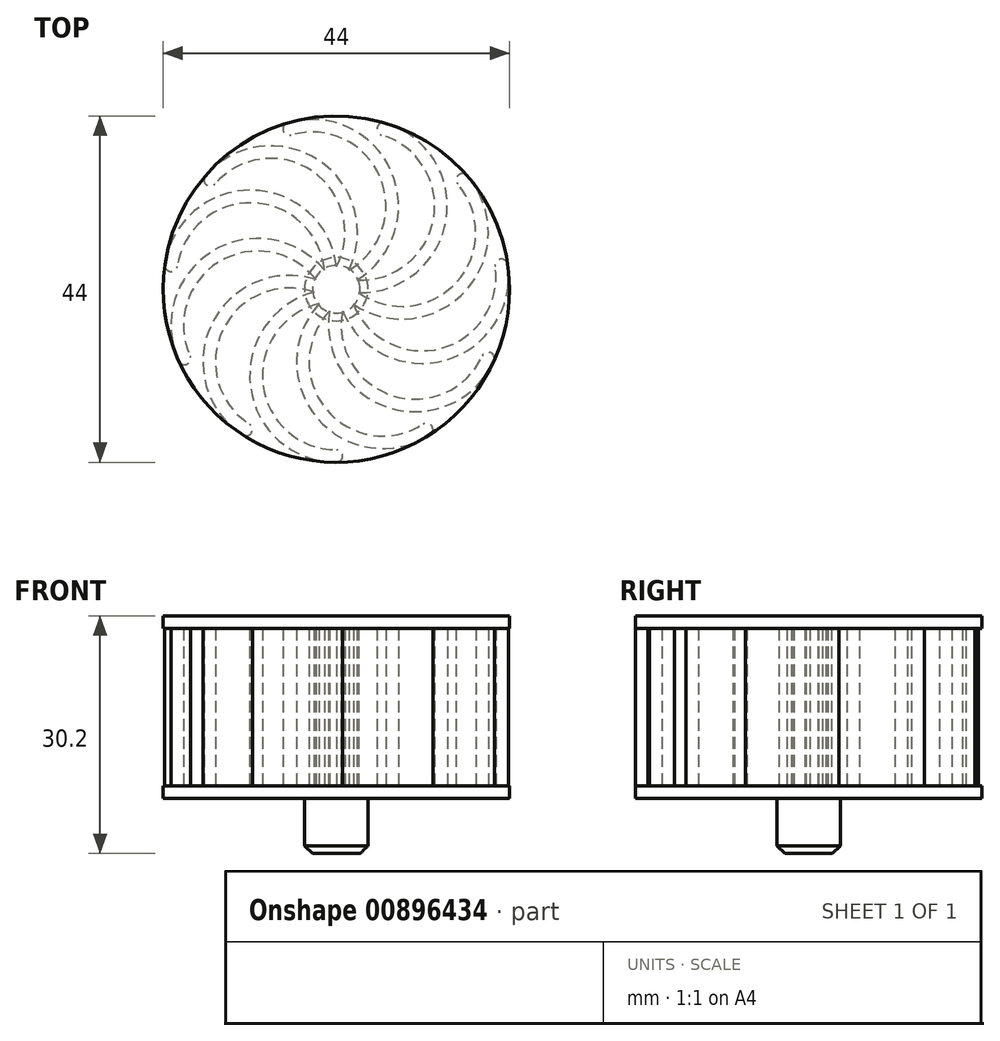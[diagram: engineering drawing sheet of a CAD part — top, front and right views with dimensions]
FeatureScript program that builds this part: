
annotation { "Feature Type Name" : "Feature", "Feature Type Description" : "" }
export const myFeature = defineFeature(function(context is Context, id is Id, definition is map)
    precondition{}
    {
        {
            assignVariable(context, id + "F0", {"name" : "mountingHeight", "anyValue" : 7 * mm});
        }
        {
            assignVariable(context, id + "F1", {"name" : "height", "anyValue" : 20 * mm});
        }
        {
            assignVariable(context, id + "F2", {"name" : "wall", "anyValue" : 1.6 * mm});
        }
        {
            assignVariable(context, id + "F3", {"name" : "blades", "anyValue" : 11});
        }
        {
            var Q0;
            Q0=qCreatedBy(makeId("Top.planeOp"),FACE);
            var sketch = newSketch(context, id + "F4", { "sketchPlane" : qUnion([Q0])});
            skCircle(sketch, "E0", {"center": v(0, 0) * mm, "radius": 22 * mm});
            skCircle(sketch, "E1", {"center": v(0, 0) * mm, "radius": 4.03 * mm});
            skSolve(sketch);
        }
        {
            var Q0;
            Q0=makeQuery(id+"F4.imprint","IMPRINT",FACE,{"disambiguationData":[TD([[makeQuery(id+"F4.imprint","IMPRINT",EDGE,{"derivedFrom":sQuery(id+"F4.wireOp",EDGE,"E0")}),1.0]])]});
            var Q1;
            Q1=makeQuery(id+"F4.imprint","IMPRINT",FACE,{"disambiguationData":[TD([[makeQuery(id+"F4.imprint","IMPRINT",EDGE,{"derivedFrom":sQuery(id+"F4.wireOp",EDGE,"E1")}),1.0]])]});
            extrude(context, id + "F5", {"entities" : qUnion([Q0, Q1]), "depth" : getVariable(context, 'wall'), "offsetDistance" : 25 * mm});
        }
        {
            var Q0;
            Q0=makeQuery(id+"F4.imprint","IMPRINT",FACE,{"disambiguationData":[TD([[makeQuery(id+"F4.imprint","IMPRINT",EDGE,{"derivedFrom":sQuery(id+"F4.wireOp",EDGE,"E1")}),1.0]])]});
            extrude(context, id + "F6", {"entities" : qUnion([Q0]), "operationType" : NewBodyOperationType.ADD, "oppositeDirection" : true, "depth" : getVariable(context, 'mountingHeight'), "offsetDistance" : 25 * mm});
        }
        {
            var Q0;
            Q0=makeQuery(id+"F5.opExtrude","CAP_FACE",FACE,{"disambiguationData":[OSD([sQuery(id+"F4.wireOp",EDGE,"E0")])],"isStart":false});
            var sketch = newSketch(context, id + "F7", { "sketchPlane" : qUnion([Q0])});
            skArc(sketch, "E2", {"start": v(0, 0) * mm, "mid": v(-11, -11) * mm, "end": v(0, -22) * mm});
            skArc(sketch, "E3.0", {"start": v(0, -1.6) * mm, "mid": v(-9.4, -11) * mm, "end": v(0, -20.4) * mm});
            skArc(sketch, "E4", {"start": v(0, 0) * mm, "mid": v(0.8, -0.8) * mm, "end": v(0, -1.6) * mm});
            skArc(sketch, "E5", {"start": v(0, -20.4) * mm, "mid": v(0.8, -21.2) * mm, "end": v(0, -22) * mm});
            skSolve(sketch);
        }
        {
            var Q0;
            Q0=makeQuery(id+"F6.opExtrude","CAP_EDGE",EDGE,{"disambiguationData":[OSD([sQuery(id+"F4.wireOp",EDGE,"E1")])],"isStart":false});
            chamfer(context, id + "F8", {"entities" : qUnion([Q0]), "width" : 1 * mm, "tangentPropagation" : true});
        }
        {
            var Q0;
            {var subQ4=sQuery(id+"F7.wireOp",EDGE,"E2");Q0=makeQuery(id+"F7.imprint","IMPRINT",FACE,{"disambiguationData":[TD([[makeQuery(id+"F7.imprint","IMPRINT",EDGE,{"derivedFrom":subQ4}),1.0]])]});}
            extrude(context, id + "F9", {"entities" : qUnion([Q0]), "depth" : getVariable(context, 'height'), "offsetDistance" : 25 * mm});
        }
        {
            var Q0;
            Q0=makeQuery(id+"F9.opExtrude","SWEPT_BODY",BODY,{"disambiguationData":[OSD([sQuery(id+"F4.wireOp",EDGE,"E0"),sQuery(id+"F7.wireOp",EDGE,"E2"),sQuery(id+"F7.wireOp",EDGE,"d03e0ac7-ecf9-454f-a7f5-ac63b770d9b9.0"),sQuery(id+"F7.wireOp",EDGE,"87743ef1-c0a4-470f-af4a-e0fff581d53f"),sQuery(id+"F7.wireOp",EDGE,"098a4024-eb5d-4de3-bc97-1e13fd1b39a1")])]});
            var Q1;
            Q1=makeQuery(id+"F6.opExtrude","SWEPT_FACE",FACE,{"disambiguationData":[OSD([sQuery(id+"F4.wireOp",EDGE,"E1")])]});
            circularPattern(context, id + "F10", {"operationType" : NewBodyOperationType.ADD, "entities" : qUnion([Q0]), "axis" : qUnion([Q1]), "angle" : 360 * degree, "instanceCount" : getVariable(context, 'blades'), "equalSpace" : true});
        }
        {
            var Q0;
            Q0=makeQuery(id+"F4.imprint","IMPRINT",FACE,{"disambiguationData":[TD([[makeQuery(id+"F4.imprint","IMPRINT",EDGE,{"derivedFrom":sQuery(id+"F4.wireOp",EDGE,"E0")}),1.0]])]});
            var Q1;
            Q1=makeQuery(id+"F4.imprint","IMPRINT",FACE,{"disambiguationData":[TD([[makeQuery(id+"F4.imprint","IMPRINT",EDGE,{"derivedFrom":sQuery(id+"F4.wireOp",EDGE,"E1")}),1.0]])]});
            extrude(context, id + "F11", {"entities" : qUnion([Q0, Q1]), "operationType" : NewBodyOperationType.ADD, "depth" : getVariable(context, 'wall') * 2 + getVariable(context, 'height'), "offsetDistance" : 25 * mm, "hasSecondDirection" : true, "secondDirectionOppositeDirection" : false, "secondDirectionDepth" : getVariable(context, 'wall') + getVariable(context, 'height')});
        }
    });
